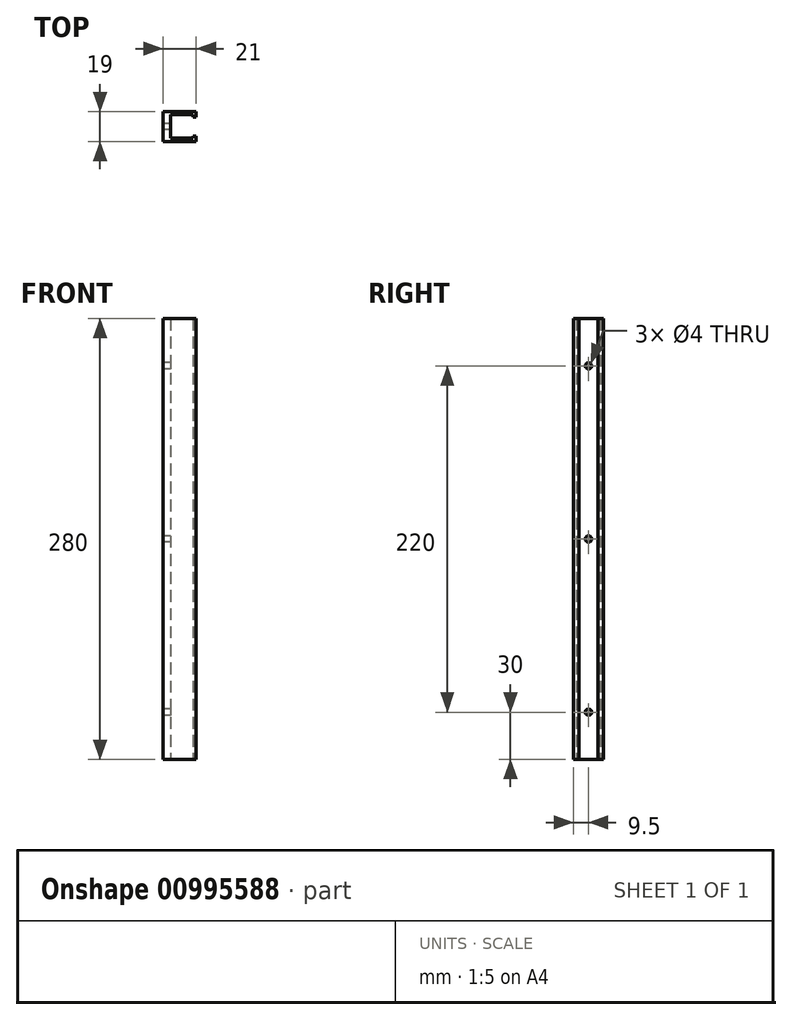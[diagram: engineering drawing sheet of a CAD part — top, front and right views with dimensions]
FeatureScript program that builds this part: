
annotation { "Feature Type Name" : "Feature", "Feature Type Description" : "" }
export const myFeature = defineFeature(function(context is Context, id is Id, definition is map)
    precondition{}
    {
        {
            var Q0;
            Q0=qCreatedBy(makeId("Front.planeOp"),FACE);
            var sketch = newSketch(context, id + "F0", { "sketchPlane" : qUnion([Q0])});
            skLineSegment(sketch, "E0.bottom", {"start": v(0, 0) * mm, "end": v(21, 0) * mm});
            skLineSegment(sketch, "E0.top", {"start": v(0, 280) * mm, "end": v(21, 280) * mm});
            skLineSegment(sketch, "E0.left", {"start": v(0, 0) * mm, "end": v(0, 280) * mm});
            skLineSegment(sketch, "E0.right", {"start": v(21, 0) * mm, "end": v(21, 280) * mm});
            skSolve(sketch);
        }
        {
            var Q0;
            Q0 = qSketchRegion(id + "F0", true);
            extrude(context, id + "F1", {"entities" : qUnion([Q0]), "depth" : 19 * mm, "offsetDistance" : 25 * mm});
        }
        {
            var Q0;
            Q0=makeQuery(id+"F1.opExtrude","SWEPT_FACE",FACE,{"disambiguationData":[OSD([sQuery(id+"F0.wireOp",EDGE,"E0.bottom")])]});
            var sketch = newSketch(context, id + "F2", { "sketchPlane" : qUnion([Q0])});
            skLineSegment(sketch, "E1.bottom", {"start": v(4.8, 17) * mm, "end": v(19, 17) * mm});
            skLineSegment(sketch, "E1.top", {"start": v(4.8, 2) * mm, "end": v(19, 2) * mm});
            skLineSegment(sketch, "E1.left", {"start": v(4.8, 17) * mm, "end": v(4.8, 2) * mm});
            skLineSegment(sketch, "E1.right", {"start": v(19, 17) * mm, "end": v(19, 15.5) * mm});
            skLineSegment(sketch, "E2", {"start": v(19, 15.5) * mm, "end": v(21, 15.5) * mm});
            skLineSegment(sketch, "E3", {"start": v(21, 15.5) * mm, "end": v(21, 3.5) * mm});
            skLineSegment(sketch, "E4", {"start": v(21, 3.5) * mm, "end": v(19, 3.5) * mm});
            skLineSegment(sketch, "E5", {"start": v(19, 3.5) * mm, "end": v(19, 2) * mm});
            skSolve(sketch);
        }
        {
            var Q0;
            Q0 = qSketchRegion(id + "F2", true);
            extrude(context, id + "F3", {"entities" : qUnion([Q0]), "operationType" : NewBodyOperationType.REMOVE, "endBound" : BoundingType.THROUGH_ALL, "oppositeDirection" : true, "depth" : 25 * mm, "offsetDistance" : 25 * mm});
        }
        {
            var Q0;
            Q0=makeQuery(id+"F1.opExtrude","SWEPT_FACE",FACE,{"disambiguationData":[OSD([sQuery(id+"F0.wireOp",EDGE,"E0.left")])]});
            var sketch = newSketch(context, id + "F4", { "sketchPlane" : qUnion([Q0])});
            skLineSegment(sketch, "E6", {"start": v(9.5, 280) * mm, "end": v(9.5, 0) * mm, "construction": true});
            skCircle(sketch, "E7", {"center": v(9.5, 30) * mm, "radius": 2 * mm});
            skCircle(sketch, "E8", {"center": v(9.5, 140) * mm, "radius": 2 * mm});
            skCircle(sketch, "E9", {"center": v(9.5, 250) * mm, "radius": 2 * mm});
            skSolve(sketch);
        }
        {
            var Q0;
            Q0 = qSketchRegion(id + "F4", true);
            extrude(context, id + "F5", {"entities" : qUnion([Q0]), "operationType" : NewBodyOperationType.REMOVE, "endBound" : BoundingType.UP_TO_NEXT, "oppositeDirection" : true, "depth" : 25 * mm, "offsetDistance" : 25 * mm});
        }
    });
